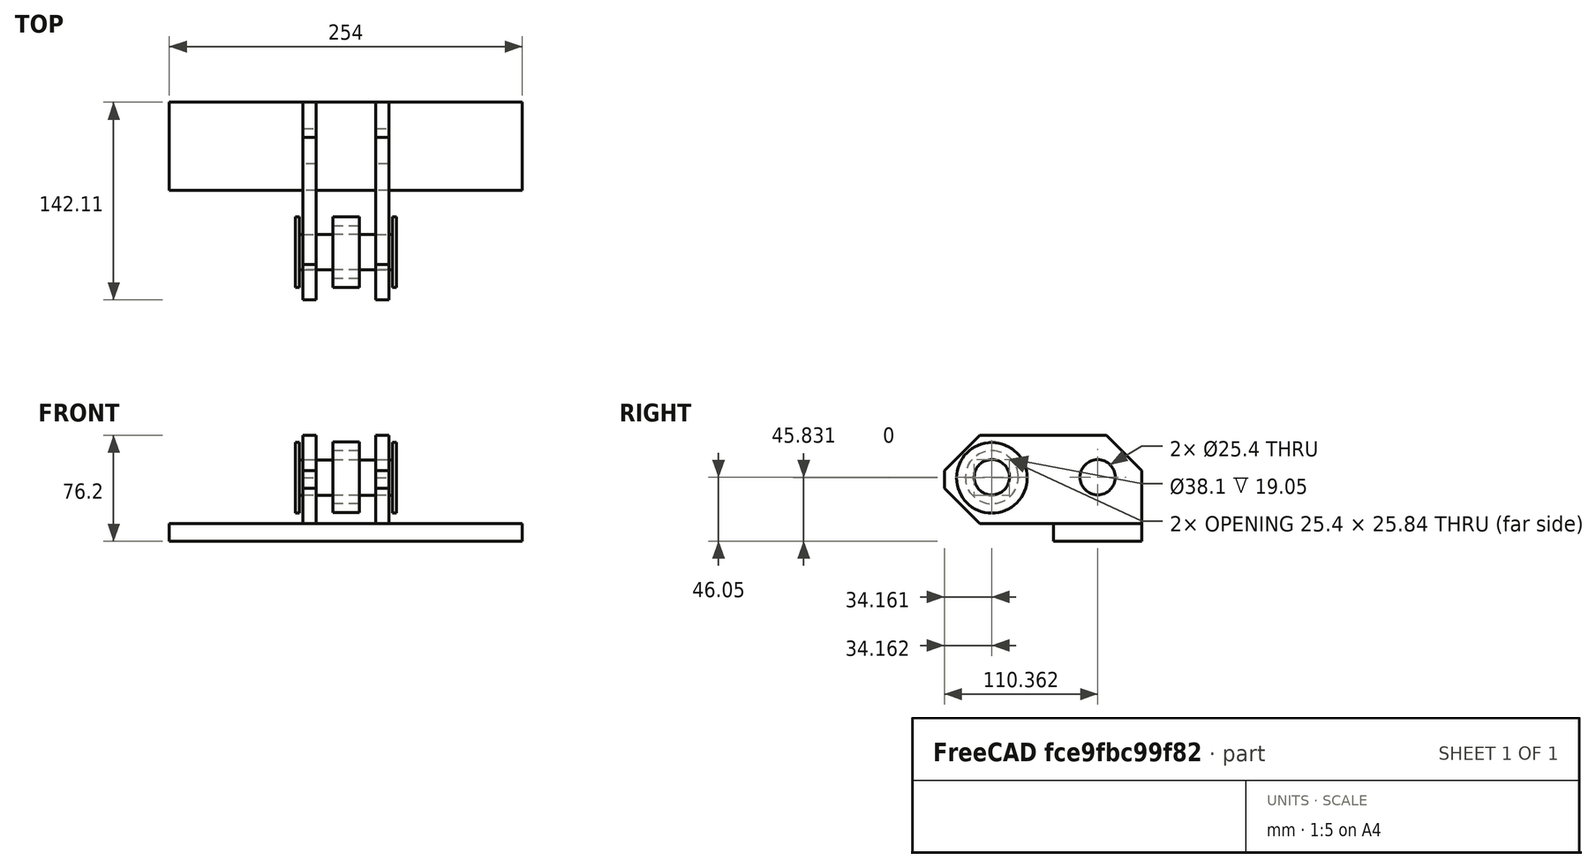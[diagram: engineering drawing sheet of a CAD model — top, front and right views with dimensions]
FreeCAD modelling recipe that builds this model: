
FCSTD DOCUMENT  (FreeCAD 0.16R6702 (Git))
Label: trackunitouterfused
License: All rights reserved
LicenseURL: http://en.wikipedia.org/wiki/All_rights_reserved
objects: App::FeaturePython×6, Part::FeaturePython×5, Part::Part2DObjectPython×1, App::DocumentObjectGroup×1, Part::MultiFuse×1
note: 7 computed .brp shape members not serialized (recipe doc carries the construction recipe); baked Part::Feature solids carry a one-line shape summary decoded from their .brp

FEATURE [Part::FeaturePython] trackpadbasic_01  # a2plus imported part (geometry in sourceFile) (typed FeaturePython)
  fixedPosition = true
  sourceFile = <userpath>/Documents/Open Source Ecology/Bulldozer/Tracks FreeCAD Files/trackpadbasic.FCStd
  timeLastImport = 1463488866
  updateColors = true
FEATURE [Part::FeaturePython] TrackChainLink_01  # a2plus imported part (geometry in sourceFile) (typed FeaturePython)
  Placement = pos=(30.9553,-24.8857,18.54) rot=(0.57735,-0.57735,-0.57735;2.0944rad)
  fixedPosition = false
  sourceFile = <userpath>/Documents/Open Source Ecology/Bulldozer/Tracks FreeCAD Files/TrackChainLink.FCStd
  timeLastImport = 1463487855
  updateColors = true
FEATURE [Part::Part2DObjectPython] Circle  # Draft 2D object (typed FeaturePython)
  FirstAngle = 0
  LastAngle = 0
  MakeFace = true
  Placement = pos=(0,60.6716,12.7) rot=(1,0,0;1.5708rad)
  Radius = 31.0261
FEATURE [App::DocumentObjectGroup] Construction
  Group = -> [Circle]
FEATURE [Part::FeaturePython] TrackChainLink_002  # a2plus imported part (geometry in sourceFile) (typed FeaturePython)
  Placement = pos=(-21.3172,-24.8857,18.54) rot=(0.57735,-0.57735,-0.57735;2.0944rad)
  fixedPosition = false
  sourceFile = <userpath>/Documents/Open Source Ecology/Bulldozer/Tracks FreeCAD Files/TrackChainLink.FCStd
  timeLastImport = 1463487855
  updateColors = true
FEATURE [Part::FeaturePython] trackroller_01  # a2plus imported part (geometry in sourceFile) (typed FeaturePython)
  Placement = pos=(-9.43522,-47.2784,46.0502) rot=(0.57735,0.57735,0.57735;2.0944rad)
  fixedPosition = false
  sourceFile = <userpath>/Documents/Open Source Ecology/Bulldozer/Tracks FreeCAD Files/trackroller.FCStd
  timeLastImport = 1463678662
  updateColors = true
FEATURE [App::FeaturePython] axialConstraint01  # a2plus constraint (typed FeaturePython)
  Object1 = TrackChainLink_01
  Object2 = trackroller_01
  SubElement1 = Face9
  SubElement2 = Face2
  Type = axial
  directionConstraint = 1
  lockRotation = false
FEATURE [App::FeaturePython] axialConstraint01_mirror  label="axialConstraint01_"  # a2plus constraint (typed FeaturePython)
  Object1 = TrackChainLink_01
  Object2 = trackroller_01
  SubElement1 = Face9
  SubElement2 = Face2
  Type = axial
  directionConstraint = 1
  lockRotation = false
FEATURE [Part::FeaturePython] trackpin_002  # a2plus imported part (geometry in sourceFile) (typed FeaturePython)
  Placement = pos=(36.5379,-47.2784,45.6115) rot=(0,-1,0;1.5708rad)
  fixedPosition = false
  sourceFile = <userpath>/Documents/Open Source Ecology/Bulldozer/Tracks FreeCAD Files/trackpin.FCStd
  timeLastImport = 1463834196
  updateColors = true
FEATURE [App::FeaturePython] axialConstraint03  # a2plus constraint (typed FeaturePython)
  Object1 = trackroller_01
  Object2 = TrackChainLink_002
  SubElement1 = Face1
  SubElement2 = Face9
  Type = axial
  directionConstraint = 1
  lockRotation = false
FEATURE [App::FeaturePython] axialConstraint03_mirror  label="axialConstraint03_"  # a2plus constraint (typed FeaturePython)
  Object1 = trackroller_01
  Object2 = TrackChainLink_002
  SubElement1 = Face1
  SubElement2 = Face9
  Type = axial
  directionConstraint = 1
  lockRotation = false
FEATURE [App::FeaturePython] axialConstraint02  # a2plus constraint (typed FeaturePython)
  Object1 = TrackChainLink_002
  Object2 = trackpin_002
  SubElement1 = Face9
  SubElement2 = Face4
  Type = axial
  directionConstraint = 1
  lockRotation = false
FEATURE [App::FeaturePython] axialConstraint02_mirror  label="axialConstraint02_"  # a2plus constraint (typed FeaturePython)
  Object1 = TrackChainLink_002
  Object2 = trackpin_002
  SubElement1 = Face9
  SubElement2 = Face4
  Type = axial
  directionConstraint = 1
  lockRotation = false
FEATURE [Part::MultiFuse] Fusion
  Shapes = -> [trackpadbasic_01,TrackChainLink_01,TrackChainLink_002,trackroller_01,trackpin_002]
